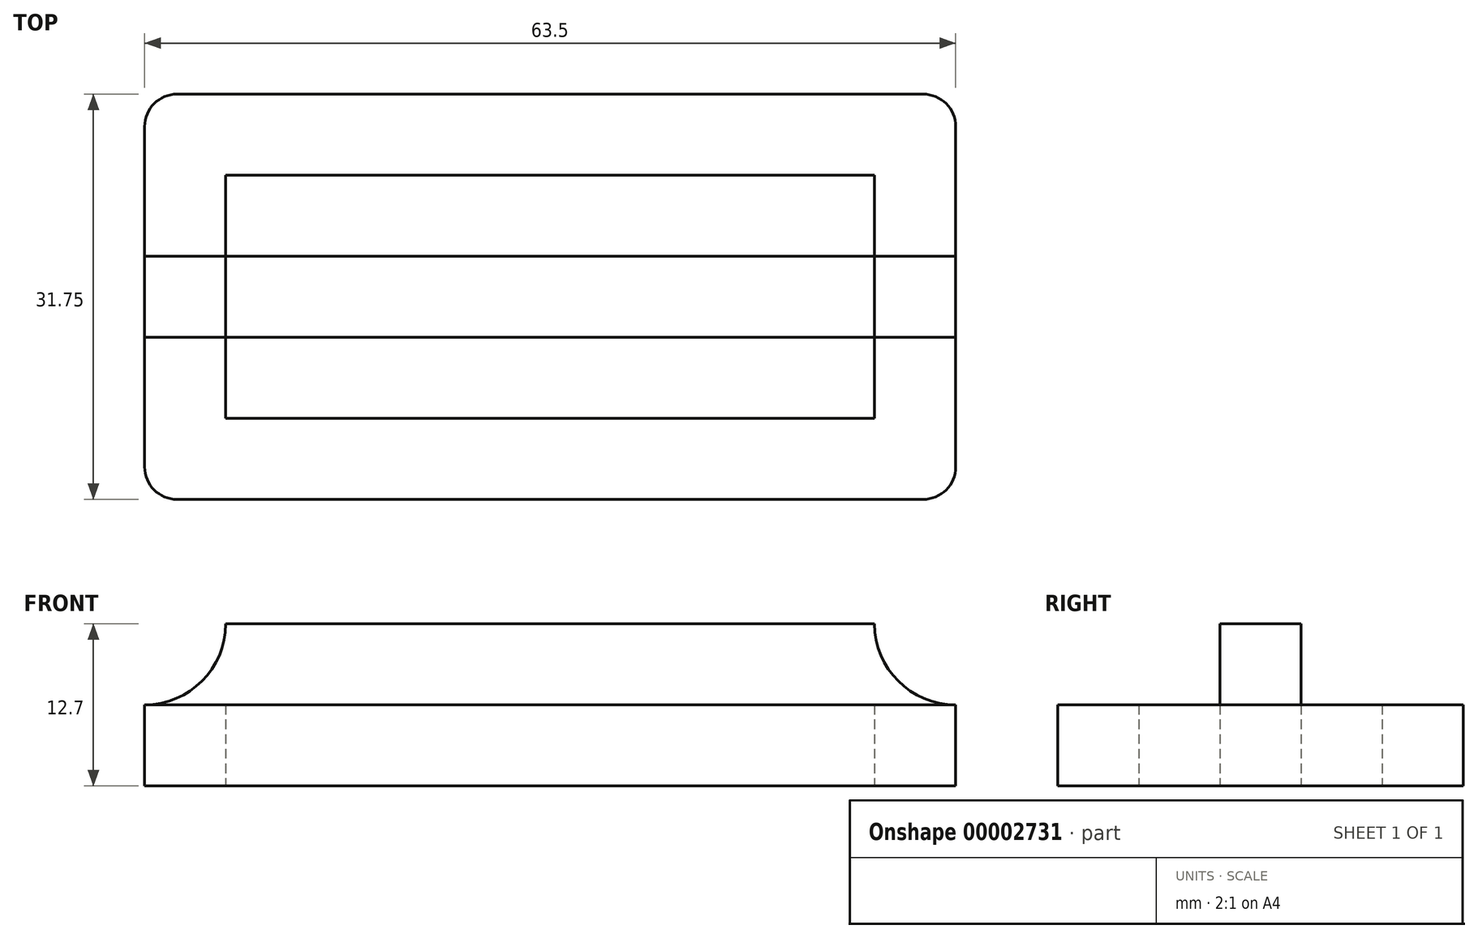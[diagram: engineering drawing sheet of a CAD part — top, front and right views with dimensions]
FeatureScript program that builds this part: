
annotation { "Feature Type Name" : "Feature", "Feature Type Description" : "" }
export const myFeature = defineFeature(function(context is Context, id is Id, definition is map)
    precondition{}
    {
        {
            var Q0;
            Q0=qCreatedBy(makeId("Top.planeOp"),FACE);
            var sketch = newSketch(context, id + "F0", { "sketchPlane" : qUnion([Q0])});
            skLineSegment(sketch, "E0.bottom", {"start": v(0, 0) * mm, "end": v(63.5, 0) * mm});
            skLineSegment(sketch, "E0.top", {"start": v(0, 31.75) * mm, "end": v(63.5, 31.75) * mm});
            skLineSegment(sketch, "E0.left", {"start": v(0, 0) * mm, "end": v(0, 31.75) * mm});
            skLineSegment(sketch, "E0.right", {"start": v(63.5, 0) * mm, "end": v(63.5, 31.75) * mm});
            skLineSegment(sketch, "E1", {"start": v(0, 0) * mm, "end": v(6.35, 0) * mm, "construction": true});
            skLineSegment(sketch, "E2", {"start": v(6.35, 0) * mm, "end": v(6.35, 6.35) * mm, "construction": true});
            skLineSegment(sketch, "E3", {"start": v(6.35, 6.35) * mm, "end": v(6.35, 12.7) * mm, "construction": true});
            skLineSegment(sketch, "E4", {"start": v(6.35, 12.7) * mm, "end": v(6.35, 19.05) * mm, "construction": true});
            skLineSegment(sketch, "E5", {"start": v(6.35, 19.05) * mm, "end": v(6.35, 25.4) * mm, "construction": true});
            skLineSegment(sketch, "E6", {"start": v(6.35, 25.4) * mm, "end": v(0, 25.4) * mm, "construction": true});
            skSolve(sketch);
        }
        {
            var Q0;
            Q0=makeQuery(id+"F0.imprint","IMPRINT",FACE,{"disambiguationData":[TD([[makeQuery(id+"F0.imprint","IMPRINT",EDGE,{"derivedFrom":sQuery(id+"F0.wireOp",EDGE,"E0.bottom")}),1.0]])]});
            var sketch = newSketch(context, id + "F1", { "sketchPlane" : qUnion([Q0])});
            skLineSegment(sketch, "E7.bottom", {"start": v(6.35, 6.35) * mm, "end": v(57.15, 6.35) * mm});
            skLineSegment(sketch, "E7.top", {"start": v(6.35, 12.7) * mm, "end": v(57.15, 12.7) * mm});
            skLineSegment(sketch, "E7.left", {"start": v(6.35, 6.35) * mm, "end": v(6.35, 12.7) * mm});
            skLineSegment(sketch, "E7.right", {"start": v(57.15, 6.35) * mm, "end": v(57.15, 12.7) * mm});
            skLineSegment(sketch, "E8.bottom", {"start": v(6.35, 19.05) * mm, "end": v(57.15, 19.05) * mm});
            skLineSegment(sketch, "E8.top", {"start": v(6.35, 25.4) * mm, "end": v(57.15, 25.4) * mm});
            skLineSegment(sketch, "E8.left", {"start": v(6.35, 19.05) * mm, "end": v(6.35, 25.4) * mm});
            skLineSegment(sketch, "E8.right", {"start": v(57.15, 19.05) * mm, "end": v(57.15, 25.4) * mm});
            skSolve(sketch);
        }
        {
            var Q0;
            Q0=makeQuery(id+"F0.imprint","IMPRINT",FACE,{"disambiguationData":[TD([[makeQuery(id+"F0.imprint","IMPRINT",EDGE,{"derivedFrom":sQuery(id+"F0.wireOp",EDGE,"E0.bottom")}),1.0]])]});
            var sketch = newSketch(context, id + "F2", { "sketchPlane" : qUnion([Q0])});
            skLineSegment(sketch, "E9.bottom", {"start": v(6.35, 12.7) * mm, "end": v(57.15, 12.7) * mm});
            skLineSegment(sketch, "E9.top", {"start": v(6.35, 19.05) * mm, "end": v(57.15, 19.05) * mm});
            skLineSegment(sketch, "E9.left", {"start": v(6.35, 12.7) * mm, "end": v(6.35, 19.05) * mm});
            skLineSegment(sketch, "E9.right", {"start": v(57.15, 12.7) * mm, "end": v(57.15, 19.05) * mm});
            skSolve(sketch);
        }
        {
            var Q0;
            Q0 = qSketchRegion(id + "F0", true);
            extrude(context, id + "F3", {"entities" : qUnion([Q0]), "depth" : 6.35 * mm});
        }
        {
            var Q0;
            Q0 = qSketchRegion(id + "F1", true);
            extrude(context, id + "F4", {"entities" : qUnion([Q0]), "operationType" : NewBodyOperationType.REMOVE, "depth" : 6.35 * mm});
        }
        {
            var Q0;
            Q0 = qSketchRegion(id + "F2", true);
            extrude(context, id + "F5", {"entities" : qUnion([Q0]), "operationType" : NewBodyOperationType.ADD, "depth" : 12.7 * mm});
        }
        {
            var Q0;
            Q0=makeQuery(id+"F5.boolean.opBoolean","INTERSECT",EDGE,{"derivedFrom":[makeQuery(id+"F3.opExtrude","CAP_FACE",FACE,{"disambiguationData":[OSD([sQuery(id+"F0.wireOp",EDGE,"E0.bottom"),sQuery(id+"F0.wireOp",EDGE,"E0.top"),sQuery(id+"F0.wireOp",EDGE,"E0.left"),sQuery(id+"F0.wireOp",EDGE,"E0.right")])],"isStart":false}),makeQuery(id+"F5.opExtrude","SWEPT_FACE",FACE,{"disambiguationData":[OSD([sQuery(id+"F2.wireOp",EDGE,"E9.right")])]})]});
            var Q1;
            Q1=makeQuery(id+"F5.boolean.opBoolean","INTERSECT",EDGE,{"derivedFrom":[makeQuery(id+"F3.opExtrude","CAP_FACE",FACE,{"disambiguationData":[OSD([sQuery(id+"F0.wireOp",EDGE,"E0.bottom"),sQuery(id+"F0.wireOp",EDGE,"E0.top"),sQuery(id+"F0.wireOp",EDGE,"E0.left"),sQuery(id+"F0.wireOp",EDGE,"E0.right")])],"isStart":false}),makeQuery(id+"F5.opExtrude","SWEPT_FACE",FACE,{"disambiguationData":[OSD([sQuery(id+"F2.wireOp",EDGE,"E9.left")])]})]});
            fillet(context, id + "F6", {"entities" : qUnion([Q0, Q1]), "radius" : 6.35 * mm, "tangentPropagation" : true, "allowEdgeOverflow" : false});
        }
        {
            var Q0;
            Q0=makeQuery(id+"F3.opExtrude","SWEPT_EDGE",EDGE,{"disambiguationData":[OSD([sQuery(id+"F0.wireOp",EDGE,"E0.bottom"),sQuery(id+"F0.wireOp",EDGE,"E0.left")])]});
            var Q1;
            Q1=makeQuery(id+"F3.opExtrude","SWEPT_EDGE",EDGE,{"disambiguationData":[OSD([sQuery(id+"F0.wireOp",EDGE,"E0.bottom"),sQuery(id+"F0.wireOp",EDGE,"E0.right")])]});
            var Q2;
            Q2=makeQuery(id+"F3.opExtrude","SWEPT_EDGE",EDGE,{"disambiguationData":[OSD([sQuery(id+"F0.wireOp",EDGE,"E0.top"),sQuery(id+"F0.wireOp",EDGE,"E0.right")])]});
            var Q3;
            Q3=makeQuery(id+"F3.opExtrude","SWEPT_EDGE",EDGE,{"disambiguationData":[OSD([sQuery(id+"F0.wireOp",EDGE,"E0.top"),sQuery(id+"F0.wireOp",EDGE,"E0.left")])]});
            fillet(context, id + "F7", {"entities" : qUnion([Q0, Q1, Q2, Q3]), "radius" : 2.54 * mm, "tangentPropagation" : true, "allowEdgeOverflow" : false});
        }
    });
